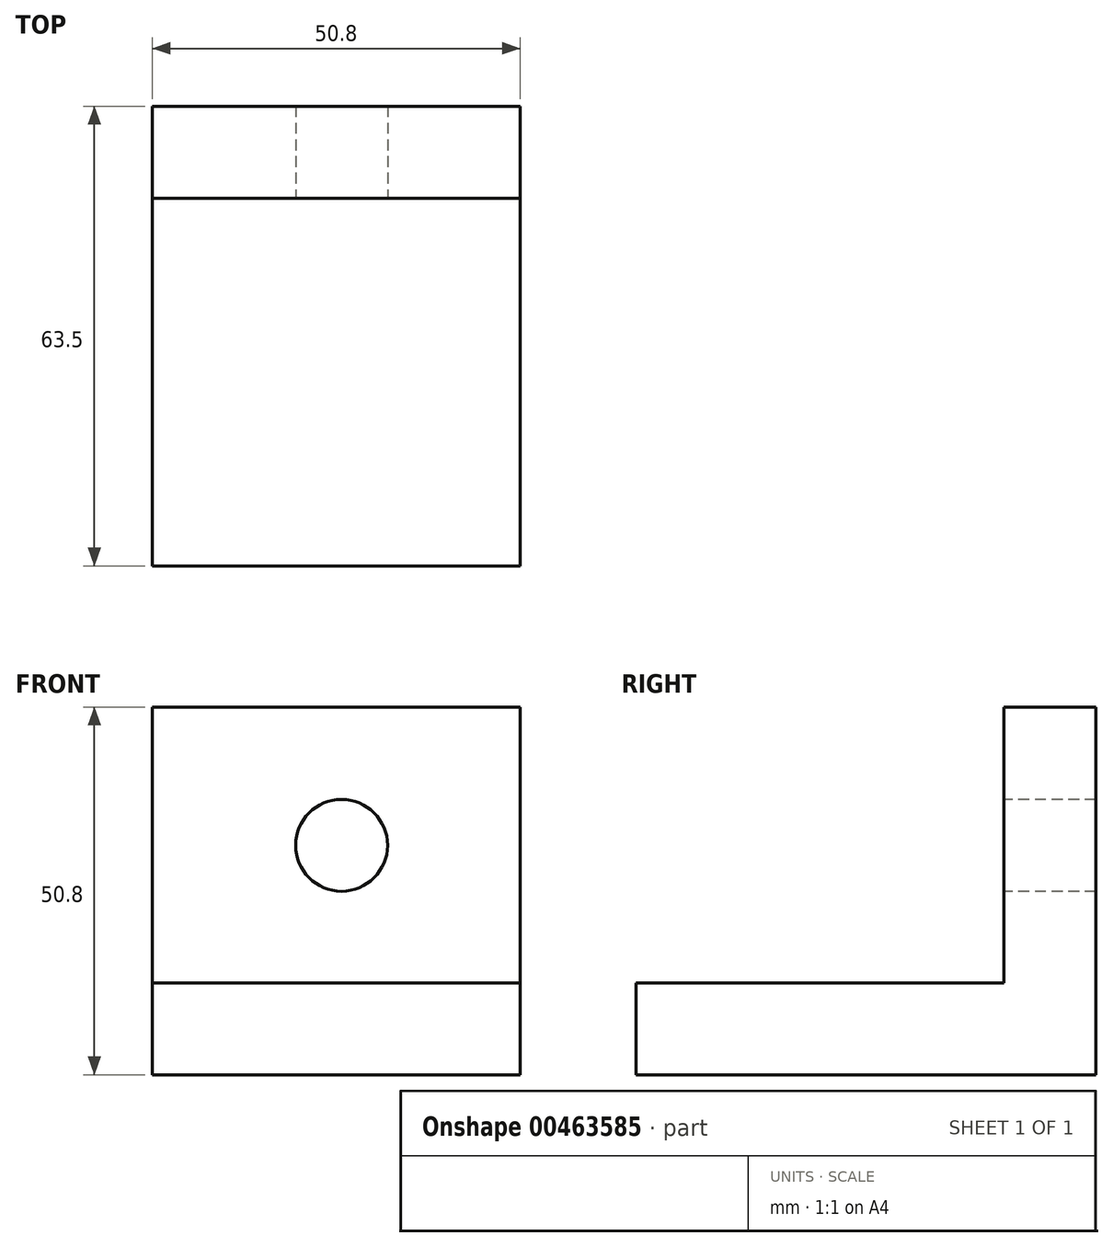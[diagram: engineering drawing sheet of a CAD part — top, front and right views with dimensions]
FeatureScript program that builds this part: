
annotation { "Feature Type Name" : "Feature", "Feature Type Description" : "" }
export const myFeature = defineFeature(function(context is Context, id is Id, definition is map)
    precondition{}
    {
        {
            var Q0;
            Q0=qCreatedBy(makeId("Front.planeOp"),FACE);
            var sketch = newSketch(context, id + "F0", { "sketchPlane" : qUnion([Q0])});
            skLineSegment(sketch, "E0.bottom", {"start": v(-32.87, 32.96) * mm, "end": v(17.93, 32.96) * mm});
            skLineSegment(sketch, "E0.top", {"start": v(-32.87, -17.84) * mm, "end": v(17.93, -17.84) * mm});
            skLineSegment(sketch, "E0.left", {"start": v(-32.87, 32.96) * mm, "end": v(-32.87, -17.84) * mm});
            skLineSegment(sketch, "E0.right", {"start": v(17.93, 32.96) * mm, "end": v(17.93, -17.84) * mm});
            skSolve(sketch);
        }
        {
            var Q0;
            Q0=makeQuery(id+"F0.imprint","IMPRINT",FACE,{"disambiguationData":[TD([[makeQuery(id+"F0.imprint","IMPRINT",EDGE,{"derivedFrom":sQuery(id+"F0.wireOp",EDGE,"E0.bottom")}),-1.0]])]});
            extrude(context, id + "F1", {"entities" : qUnion([Q0]), "depth" : 12.7 * mm});
        }
        {
            var Q0;
            Q0=makeQuery(id+"F1.opExtrude","CAP_FACE",FACE,{"disambiguationData":[OSD([sQuery(id+"F0.wireOp",EDGE,"E0.bottom"),sQuery(id+"F0.wireOp",EDGE,"E0.top"),sQuery(id+"F0.wireOp",EDGE,"E0.left"),sQuery(id+"F0.wireOp",EDGE,"E0.right")])],"isStart":false});
            var sketch = newSketch(context, id + "F2", { "sketchPlane" : qUnion([Q0])});
            skCircle(sketch, "E1", {"center": v(-6.74, 13.85) * mm, "radius": 6.35 * mm});
            skSolve(sketch);
        }
        {
            var Q0;
            Q0=sQuery(id+"F2.wireOp",VERTEX,"E1.center");
            var Q1;
            Q1=makeQuery(id+"F1.opExtrude","SWEPT_BODY",BODY,{"disambiguationData":[OSD([sQuery(id+"F0.wireOp",EDGE,"E0.bottom"),sQuery(id+"F0.wireOp",EDGE,"E0.top"),sQuery(id+"F0.wireOp",EDGE,"E0.left"),sQuery(id+"F0.wireOp",EDGE,"E0.right")])]});
            hole(context, id + "F3", {"style" : HoleStyle.SIMPLE, "endStyle" : HoleEndStyle.THROUGH, "holeDiameter" : 12.7 * mm, "isTappedThrough" : true, "tappedDepth" : 12.7 * mm, "tapClearance" : 3, "locations" : qUnion([Q0]), "scope" : qUnion([Q1])});
        }
        {
            var Q0;
            Q0=makeQuery(id+"F1.opExtrude","CAP_FACE",FACE,{"disambiguationData":[OSD([sQuery(id+"F0.wireOp",EDGE,"E0.bottom"),sQuery(id+"F0.wireOp",EDGE,"E0.top"),sQuery(id+"F0.wireOp",EDGE,"E0.left"),sQuery(id+"F0.wireOp",EDGE,"E0.right")])],"isStart":false});
            var sketch = newSketch(context, id + "F4", { "sketchPlane" : qUnion([Q0])});
            skLineSegment(sketch, "E2.bottom", {"start": v(-32.87, -17.84) * mm, "end": v(17.93, -17.84) * mm});
            skLineSegment(sketch, "E2.top", {"start": v(-32.87, -5.14) * mm, "end": v(17.93, -5.14) * mm});
            skLineSegment(sketch, "E2.left", {"start": v(-32.87, -17.84) * mm, "end": v(-32.87, -5.14) * mm});
            skLineSegment(sketch, "E2.right", {"start": v(17.93, -17.84) * mm, "end": v(17.93, -5.14) * mm});
            skSolve(sketch);
        }
        {
            var Q0;
            Q0=makeQuery(id+"F4.imprint","IMPRINT",FACE,{"disambiguationData":[TD([[makeQuery(id+"F4.imprint","IMPRINT",EDGE,{"derivedFrom":sQuery(id+"F4.wireOp",EDGE,"E2.bottom")}),1.0]])]});
            extrude(context, id + "F5", {"entities" : qUnion([Q0]), "operationType" : NewBodyOperationType.ADD, "depth" : 50.8 * mm});
        }
    });
